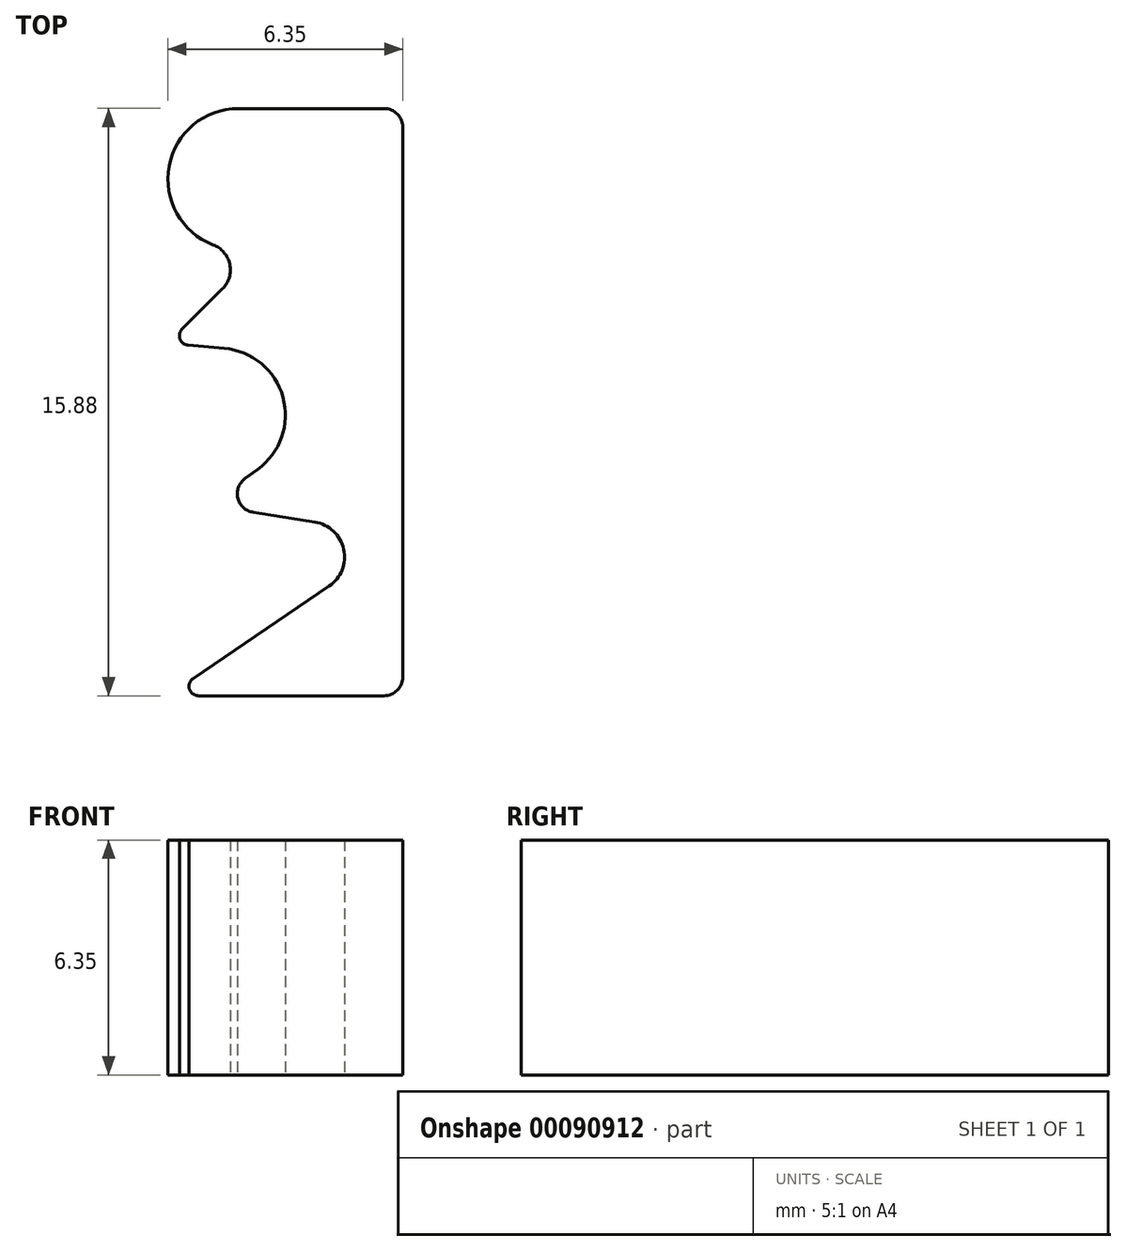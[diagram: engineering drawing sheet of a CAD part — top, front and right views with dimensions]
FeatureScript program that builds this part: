
annotation { "Feature Type Name" : "Feature", "Feature Type Description" : "" }
export const myFeature = defineFeature(function(context is Context, id is Id, definition is map)
    precondition{}
    {
        {
            var Q0;
            Q0=qCreatedBy(makeId("Top.planeOp"),FACE);
            var sketch = newSketch(context, id + "F0", { "sketchPlane" : qUnion([Q0])});
            skLineSegment(sketch, "E0.bottom", {"start": v(0.83, 0) * mm, "end": v(5.84, 0) * mm});
            skLineSegment(sketch, "E0.top", {"start": v(1.9, 15.88) * mm, "end": v(5.84, 15.88) * mm});
            skLineSegment(sketch, "E0.left", {"start": v(0, 0) * mm, "end": v(0, 13.97) * mm, "construction": true});
            skLineSegment(sketch, "E0.right", {"start": v(6.35, 0.5) * mm, "end": v(6.35, 15.37) * mm});
            skLineSegment(sketch, "E1", {"start": v(0, 15.88) * mm, "end": v(6.35, 0) * mm, "construction": true});
            skLineSegment(sketch, "E2", {"start": v(1.48, 11) * mm, "end": v(0.39, 9.91) * mm});
            skLineSegment(sketch, "E3", {"start": v(0.54, 9.48) * mm, "end": v(1.52, 9.4) * mm});
            skLineSegment(sketch, "E4", {"start": v(2.43, 6.12) * mm, "end": v(2.09, 5.87) * mm});
            skLineSegment(sketch, "E5", {"start": v(2.3, 4.96) * mm, "end": v(3.97, 4.7) * mm});
            skLineSegment(sketch, "E6", {"start": v(4.36, 2.96) * mm, "end": v(0.68, 0.46) * mm});
            skPoint(sketch, "E7.visualSharp", {"position": v(0, 15.88) * mm});
            skArc(sketch, "E7.filletArc", {"start": v(1.9, 15.88) * mm, "mid": v(0.03, 14.32) * mm, "end": v(1.22, 12.2) * mm});
            skArc(sketch, "E8", {"start": v(1.48, 11) * mm, "mid": v(1.67, 11.66) * mm, "end": v(1.22, 12.2) * mm});
            skPoint(sketch, "E9.visualSharp", {"position": v(0, 9.52) * mm});
            skArc(sketch, "E9.filletArc", {"start": v(0.39, 9.91) * mm, "mid": v(0.33, 9.64) * mm, "end": v(0.54, 9.48) * mm});
            skArc(sketch, "E10", {"start": v(2.43, 6.12) * mm, "mid": v(3.1, 8.07) * mm, "end": v(1.52, 9.4) * mm});
            skArc(sketch, "E11.filletArc", {"start": v(2.09, 5.87) * mm, "mid": v(1.9, 5.34) * mm, "end": v(2.3, 4.96) * mm});
            skArc(sketch, "E12", {"start": v(4.36, 2.96) * mm, "mid": v(4.75, 3.96) * mm, "end": v(3.97, 4.7) * mm});
            skPoint(sketch, "E13.orphan", {"position": v(6.35, 4.32) * mm});
            skPoint(sketch, "E14.visualSharp", {"position": v(0, 0) * mm});
            skArc(sketch, "E14.filletArc", {"start": v(0.68, 0.46) * mm, "mid": v(0.58, 0.18) * mm, "end": v(0.83, 0) * mm});
            skPoint(sketch, "E15.visualSharp", {"position": v(6.35, 0) * mm});
            skArc(sketch, "E15.filletArc", {"start": v(5.84, 0) * mm, "mid": v(6.2, 0.15) * mm, "end": v(6.35, 0.5) * mm});
            skPoint(sketch, "E16.visualSharp", {"position": v(6.35, 15.88) * mm});
            skArc(sketch, "E16.filletArc", {"start": v(6.35, 15.37) * mm, "mid": v(6.2, 15.73) * mm, "end": v(5.84, 15.88) * mm});
            skSolve(sketch);
        }
        {
            var Q0;
            Q0=makeQuery(id+"F0.imprint","IMPRINT",FACE,{"disambiguationData":[TD([[makeQuery(id+"F0.imprint","IMPRINT",EDGE,{"derivedFrom":sQuery(id+"F0.wireOp",EDGE,"E0.bottom")}),1.0]])]});
            extrude(context, id + "F1", {"entities" : qUnion([Q0]), "depth" : 6.35 * mm});
        }
    });
